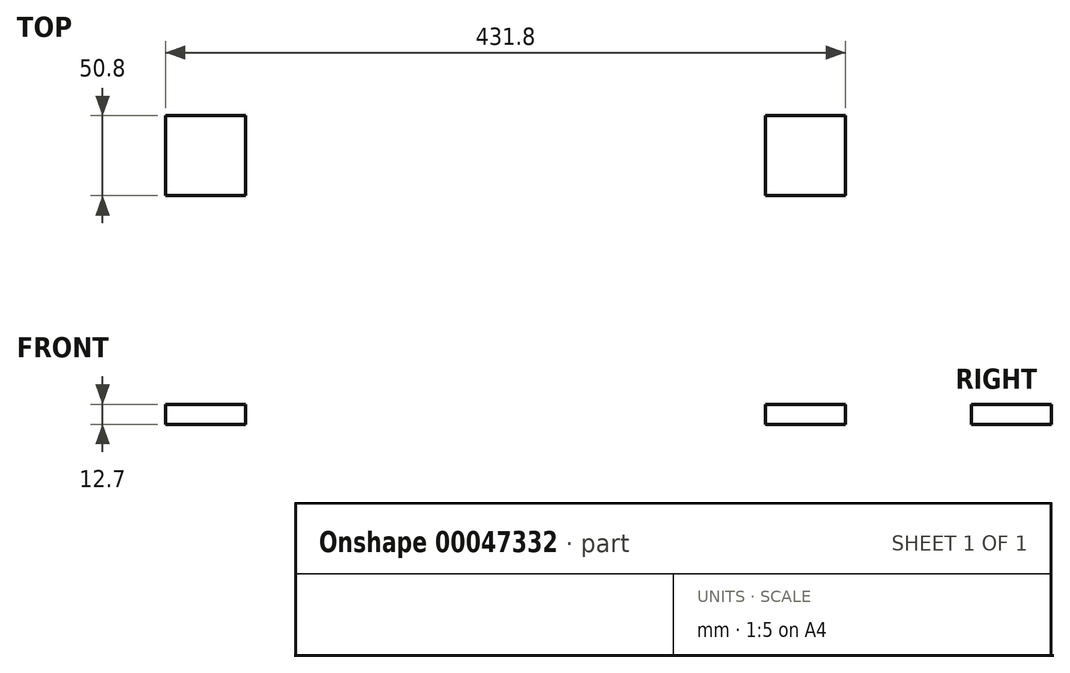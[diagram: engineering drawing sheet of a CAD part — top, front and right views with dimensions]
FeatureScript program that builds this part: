
annotation { "Feature Type Name" : "Feature", "Feature Type Description" : "" }
export const myFeature = defineFeature(function(context is Context, id is Id, definition is map)
    precondition{}
    {
        {
            var Q0;
            Q0=qCreatedBy(makeId("Top.planeOp"),FACE);
            var sketch = newSketch(context, id + "F0", { "sketchPlane" : qUnion([Q0])});
            skLineSegment(sketch, "E0.bottom", {"start": v(-36.94, 313.7) * mm, "end": v(394.86, 313.7) * mm});
            skLineSegment(sketch, "E0.top", {"start": v(-36.94, -16.5) * mm, "end": v(394.86, -16.5) * mm});
            skLineSegment(sketch, "E0.left", {"start": v(-36.94, 313.7) * mm, "end": v(-36.94, -16.5) * mm});
            skLineSegment(sketch, "E0.right", {"start": v(394.86, 313.7) * mm, "end": v(394.86, -16.5) * mm});
            skLineSegment(sketch, "E1.bottom", {"start": v(-36.94, 313.7) * mm, "end": v(13.86, 313.7) * mm});
            skLineSegment(sketch, "E1.top", {"start": v(-36.94, 262.9) * mm, "end": v(13.86, 262.9) * mm});
            skLineSegment(sketch, "E1.left", {"start": v(-36.94, 313.7) * mm, "end": v(-36.94, 262.9) * mm});
            skLineSegment(sketch, "E1.right", {"start": v(13.86, 313.7) * mm, "end": v(13.86, 262.9) * mm});
            skLineSegment(sketch, "E2.bottom", {"start": v(-36.94, -16.5) * mm, "end": v(13.86, -16.5) * mm});
            skLineSegment(sketch, "E2.top", {"start": v(-36.94, 34.3) * mm, "end": v(13.86, 34.3) * mm});
            skLineSegment(sketch, "E2.left", {"start": v(-36.94, -16.5) * mm, "end": v(-36.94, 34.3) * mm});
            skLineSegment(sketch, "E2.right", {"start": v(13.86, -16.5) * mm, "end": v(13.86, 34.3) * mm});
            skLineSegment(sketch, "E3.bottom", {"start": v(394.86, 313.7) * mm, "end": v(344.06, 313.7) * mm});
            skLineSegment(sketch, "E3.top", {"start": v(394.86, 262.9) * mm, "end": v(344.06, 262.9) * mm});
            skLineSegment(sketch, "E3.left", {"start": v(394.86, 313.7) * mm, "end": v(394.86, 262.9) * mm});
            skLineSegment(sketch, "E3.right", {"start": v(344.06, 313.7) * mm, "end": v(344.06, 262.9) * mm});
            skLineSegment(sketch, "E4.bottom", {"start": v(394.86, -16.5) * mm, "end": v(344.06, -16.5) * mm});
            skLineSegment(sketch, "E4.top", {"start": v(394.86, 34.3) * mm, "end": v(344.06, 34.3) * mm});
            skLineSegment(sketch, "E4.left", {"start": v(394.86, -16.5) * mm, "end": v(394.86, 34.3) * mm});
            skLineSegment(sketch, "E4.right", {"start": v(344.06, -16.5) * mm, "end": v(344.06, 34.3) * mm});
            skSolve(sketch);
        }
        {
            var Q0;
            Q0=makeQuery(id+"F0.imprint","IMPRINT",FACE,{"disambiguationData":[TD([[makeQuery(id+"F0.imprint","IMPRINT",EDGE,{"derivedFrom":sQuery(id+"F0.wireOp",EDGE,"E0.bottom")}),-1.0]])]});
            extrude(context, id + "F1", {"entities" : qUnion([Q0]), "depth" : 12.7 * mm});
        }
        {
            var Q0;
            Q0=makeQuery(id+"F1.opExtrude","CAP_FACE",FACE,{"disambiguationData":[OSD([sQuery(id+"F0.wireOp",EDGE,"E0.bottom"),sQuery(id+"F0.wireOp",EDGE,"E0.top"),sQuery(id+"F0.wireOp",EDGE,"E0.left"),sQuery(id+"F0.wireOp",EDGE,"E0.right"),sQuery(id+"F0.wireOp",EDGE,"E1.top"),sQuery(id+"F0.wireOp",EDGE,"E1.right"),sQuery(id+"F0.wireOp",EDGE,"E2.top"),sQuery(id+"F0.wireOp",EDGE,"E2.right"),sQuery(id+"F0.wireOp",EDGE,"E3.top"),sQuery(id+"F0.wireOp",EDGE,"E3.right"),sQuery(id+"F0.wireOp",EDGE,"E4.top"),sQuery(id+"F0.wireOp",EDGE,"E4.right")])],"isStart":false});
            var sketch = newSketch(context, id + "F2", { "sketchPlane" : qUnion([Q0])});
            skCircle(sketch, "E5", {"center": v(178.96, 148.6) * mm, "radius": 127 * mm});
            skSolve(sketch);
        }
        {
            var Q0;
            Q0=sQuery(id+"F2.wireOp",VERTEX,"E5.center");
            var Q1;
            Q1=makeQuery(id+"F1.opExtrude","SWEPT_BODY",BODY,{"disambiguationData":[OSD([sQuery(id+"F0.wireOp",EDGE,"E0.bottom"),sQuery(id+"F0.wireOp",EDGE,"E0.top"),sQuery(id+"F0.wireOp",EDGE,"E0.left"),sQuery(id+"F0.wireOp",EDGE,"E0.right"),sQuery(id+"F0.wireOp",EDGE,"E1.top"),sQuery(id+"F0.wireOp",EDGE,"E1.right"),sQuery(id+"F0.wireOp",EDGE,"E2.top"),sQuery(id+"F0.wireOp",EDGE,"E2.right"),sQuery(id+"F0.wireOp",EDGE,"E3.top"),sQuery(id+"F0.wireOp",EDGE,"E3.right"),sQuery(id+"F0.wireOp",EDGE,"E4.top"),sQuery(id+"F0.wireOp",EDGE,"E4.right")])]});
            hole(context, id + "F3", {"style" : HoleStyle.SIMPLE, "holeDiameter" : 254 * mm, "endStyle" : HoleEndStyle.THROUGH, "locations" : qUnion([Q0]), "scope" : qUnion([Q1])});
        }
    });
